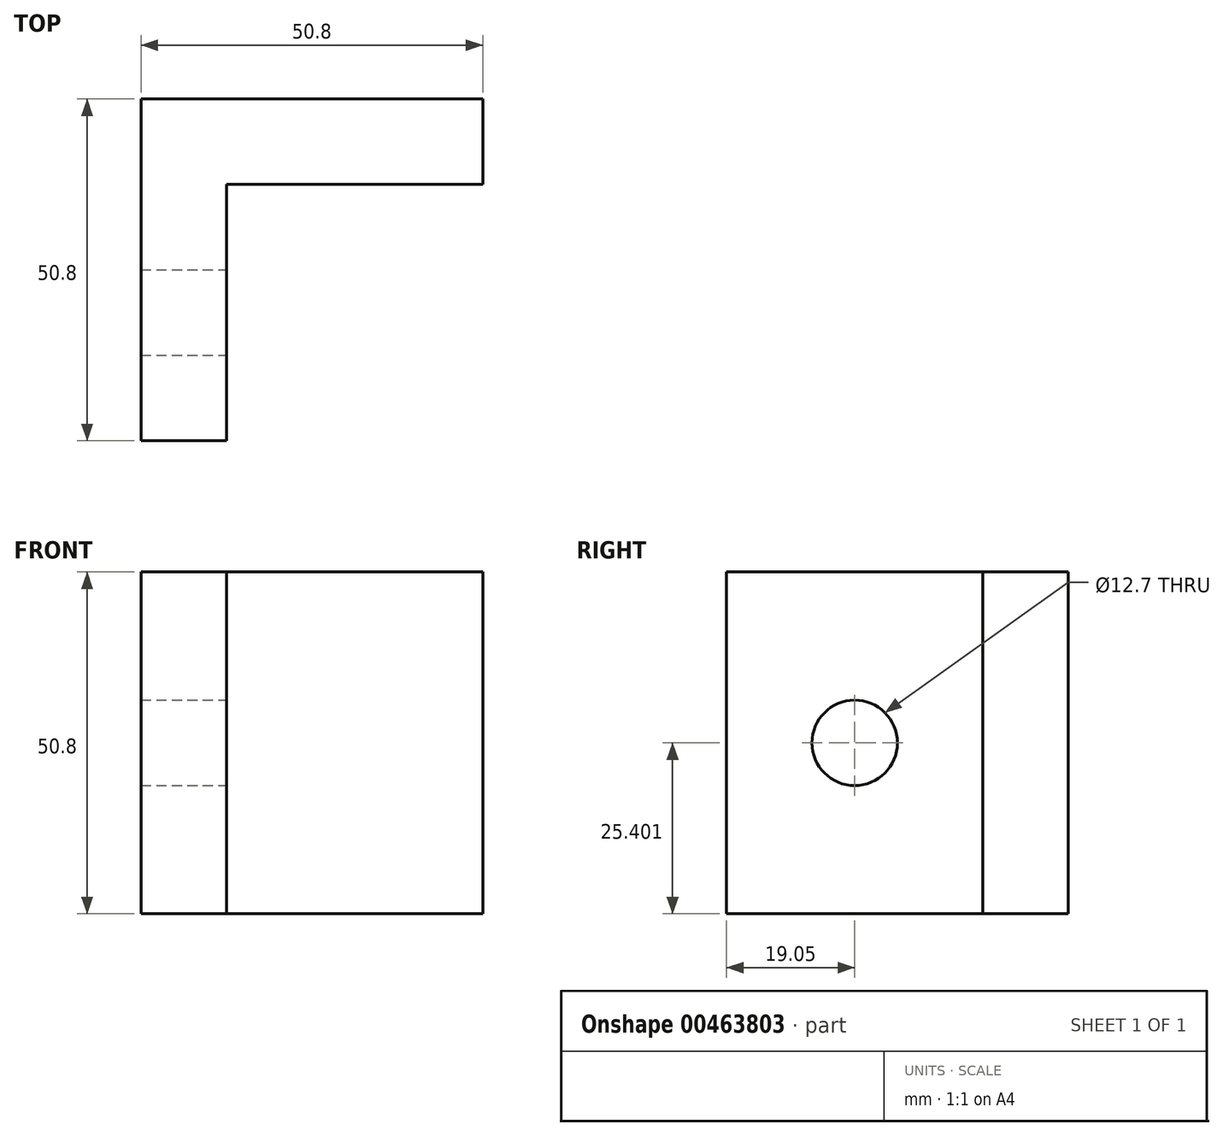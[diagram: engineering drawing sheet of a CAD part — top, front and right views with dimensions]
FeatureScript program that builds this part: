
annotation { "Feature Type Name" : "Feature", "Feature Type Description" : "" }
export const myFeature = defineFeature(function(context is Context, id is Id, definition is map)
    precondition{}
    {
        {
            var Q0;
            Q0=qCreatedBy(makeId("Front.planeOp"),FACE);
            var sketch = newSketch(context, id + "F0", { "sketchPlane" : qUnion([Q0])});
            skLineSegment(sketch, "E0.bottom", {"start": v(-41.85, 44.36) * mm, "end": v(8.95, 44.36) * mm});
            skLineSegment(sketch, "E0.top", {"start": v(-41.85, -6.44) * mm, "end": v(8.95, -6.44) * mm});
            skLineSegment(sketch, "E0.left", {"start": v(-41.85, 44.36) * mm, "end": v(-41.85, -6.44) * mm});
            skLineSegment(sketch, "E0.right", {"start": v(8.95, 44.36) * mm, "end": v(8.95, -6.44) * mm});
            skSolve(sketch);
        }
        {
            var Q0;
            Q0=makeQuery(id+"F0.imprint","IMPRINT",FACE,{"disambiguationData":[TD([[makeQuery(id+"F0.imprint","IMPRINT",EDGE,{"derivedFrom":sQuery(id+"F0.wireOp",EDGE,"E0.bottom")}),-1.0]])]});
            extrude(context, id + "F1", {"entities" : qUnion([Q0]), "depth" : 12.7 * mm});
        }
        {
            var Q0;
            Q0=makeQuery(id+"F1.opExtrude","CAP_FACE",FACE,{"disambiguationData":[OSD([sQuery(id+"F0.wireOp",EDGE,"E0.bottom"),sQuery(id+"F0.wireOp",EDGE,"E0.top"),sQuery(id+"F0.wireOp",EDGE,"E0.left"),sQuery(id+"F0.wireOp",EDGE,"E0.right")])],"isStart":false});
            var sketch = newSketch(context, id + "F2", { "sketchPlane" : qUnion([Q0])});
            skLineSegment(sketch, "E1", {"start": v(-29.15, 44.36) * mm, "end": v(-29.15, -6.44) * mm});
            skLineSegment(sketch, "E2", {"start": v(-29.15, 44.36) * mm, "end": v(-41.85, 44.36) * mm});
            skLineSegment(sketch, "E3", {"start": v(-41.85, -6.44) * mm, "end": v(-29.15, -6.44) * mm});
            skLineSegment(sketch, "E4", {"start": v(-41.85, -6.44) * mm, "end": v(-41.85, 44.36) * mm});
            skSolve(sketch);
        }
        {
            var Q0;
            Q0=makeQuery(id+"F2.imprint","IMPRINT",FACE,{"disambiguationData":[TD([[makeQuery(id+"F2.imprint","IMPRINT",EDGE,{"derivedFrom":sQuery(id+"F2.wireOp",EDGE,"E1")}),-1.0]])]});
            extrude(context, id + "F3", {"entities" : qUnion([Q0]), "operationType" : NewBodyOperationType.ADD, "depth" : 38.1 * mm});
        }
        {
            var Q0;
            Q0=makeQuery(id+"F3.opExtrude","SWEPT_FACE",FACE,{"disambiguationData":[OSD([sQuery(id+"F2.wireOp",EDGE,"E1")])]});
            var sketch = newSketch(context, id + "F4", { "sketchPlane" : qUnion([Q0])});
            skCircle(sketch, "E5", {"center": v(-31.75, 18.96) * mm, "radius": 6.35 * mm});
            skSolve(sketch);
        }
        {
            var Q0;
            Q0=makeQuery(id+"F4.imprint","IMPRINT",FACE,{"disambiguationData":[TD([[makeQuery(id+"F4.imprint","IMPRINT",EDGE,{"derivedFrom":sQuery(id+"F4.wireOp",EDGE,"E5")}),1.0]])]});
            var Q1;
            Q1=sQuery(id+"F4.wireOp",EDGE,"E5");
            extrude(context, id + "F5", {"entities" : qUnion([Q0]), "operationType" : NewBodyOperationType.REMOVE, "surfaceEntities" : qUnion([Q1]), "oppositeDirection" : true, "depth" : 25.4 * mm});
        }
    });
